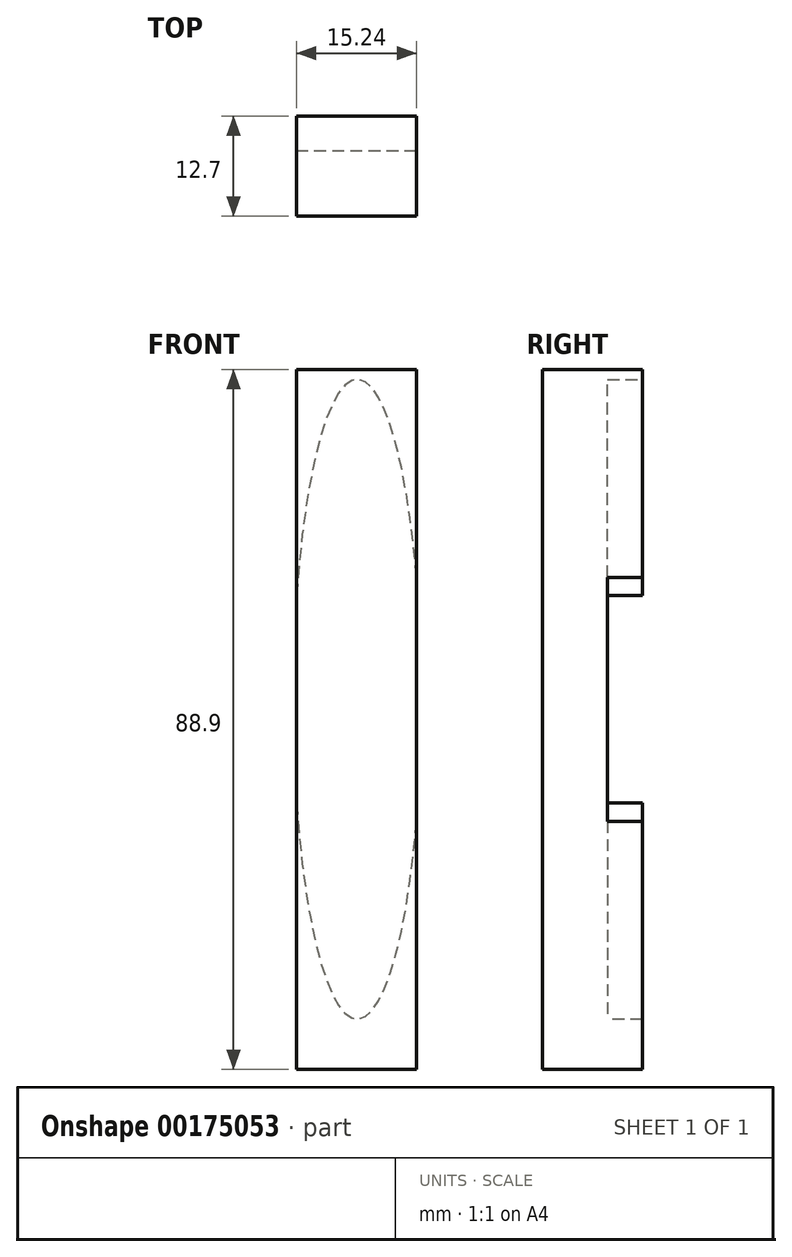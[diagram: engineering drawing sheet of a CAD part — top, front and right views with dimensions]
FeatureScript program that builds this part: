
annotation { "Feature Type Name" : "Feature", "Feature Type Description" : "" }
export const myFeature = defineFeature(function(context is Context, id is Id, definition is map)
    precondition{}
    {
        {
            var Q0;
            Q0=qCreatedBy(makeId("Front.planeOp"),FACE);
            var sketch = newSketch(context, id + "F0", { "sketchPlane" : qUnion([Q0])});
            skLineSegment(sketch, "E0.bottom", {"start": v(-15.24, 41.88) * mm, "end": v(0, 41.88) * mm});
            skLineSegment(sketch, "E0.top", {"start": v(-15.24, -47.02) * mm, "end": v(0, -47.02) * mm});
            skLineSegment(sketch, "E0.left", {"start": v(-15.24, 41.88) * mm, "end": v(-15.24, -47.02) * mm});
            skLineSegment(sketch, "E0.right", {"start": v(0, 41.88) * mm, "end": v(0, -47.02) * mm});
            skSolve(sketch);
        }
        {
            var Q0;
            Q0 = qSketchRegion(id + "F0", true);
            extrude(context, id + "F1", {"entities" : qUnion([Q0]), "depth" : 12.7 * mm});
        }
        {
            var Q0;
            Q0=qCreatedBy(makeId("Front.planeOp"),FACE);
            var sketch = newSketch(context, id + "F2", { "sketchPlane" : qUnion([Q0])});
            skEllipse(sketch, "E1", {"center": v(-7.53, 0) * mm, "majorRadius": 40.64 * mm, "minorRadius": 8.15 * mm, "majorAxis": v(0, -1)});
            skSolve(sketch);
        }
        {
            var Q0;
            Q0 = qSketchRegion(id + "F2", true);
            extrude(context, id + "F3", {"entities" : qUnion([Q0]), "operationType" : NewBodyOperationType.REMOVE, "endBound" : BoundingType.SYMMETRIC, "oppositeDirection" : true, "depth" : 8.9 * mm});
        }
    });
